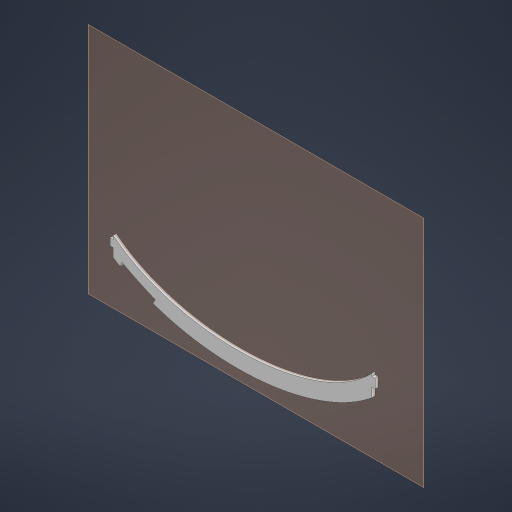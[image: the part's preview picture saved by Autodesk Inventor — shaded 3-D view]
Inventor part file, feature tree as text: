
AUTODESK INVENTOR PART (.ipt)
format: ipt  version: 2023 (Build 270158000, 158)  size: 249,856 bytes
history: native  units: mm
features: other x5, extrude x2, sketch x2, plane x1, reference x1
ambient origin geometry x8: Origin, YZ Plane, XZ Plane, XY Plane, X Axis, Y Axis, Z Axis, Center Point
bodies: Solid1 (feature_tree)
feature tree (11):
  plane  "Work Plane1"
  extrude  "Extrusion1"  Depth=15.0mm
  extrude  "Extrusion2"  Depth=3.0mm
  sketch  "Sketch1"  dims[d0=15.0mm d1=15.0mm]
  reference  "Reference1"
  sketch  "Sketch2"  dims[d2=3.0mm d3=0.0mm d5=3.0mm d6=3.0mm d7=6.0mm d8=6.0mm d9=3.0mm d10=3.0mm d11=6.0mm d12=6.0mm d13=10.0mm d14=0.0mm]
  parser-record x1  (decoder bookkeeping rows leaked as tree rows — omitted from the tree; the rows remain in map.json)
  other  "Assembly1.iam"
  other  "lower_centering_ring:1"
  other  "Assembly1"
  other  "vase_v2._tom:1"
note: 1 file-system path scrubbed to <path> (originals preserved in map.json)
